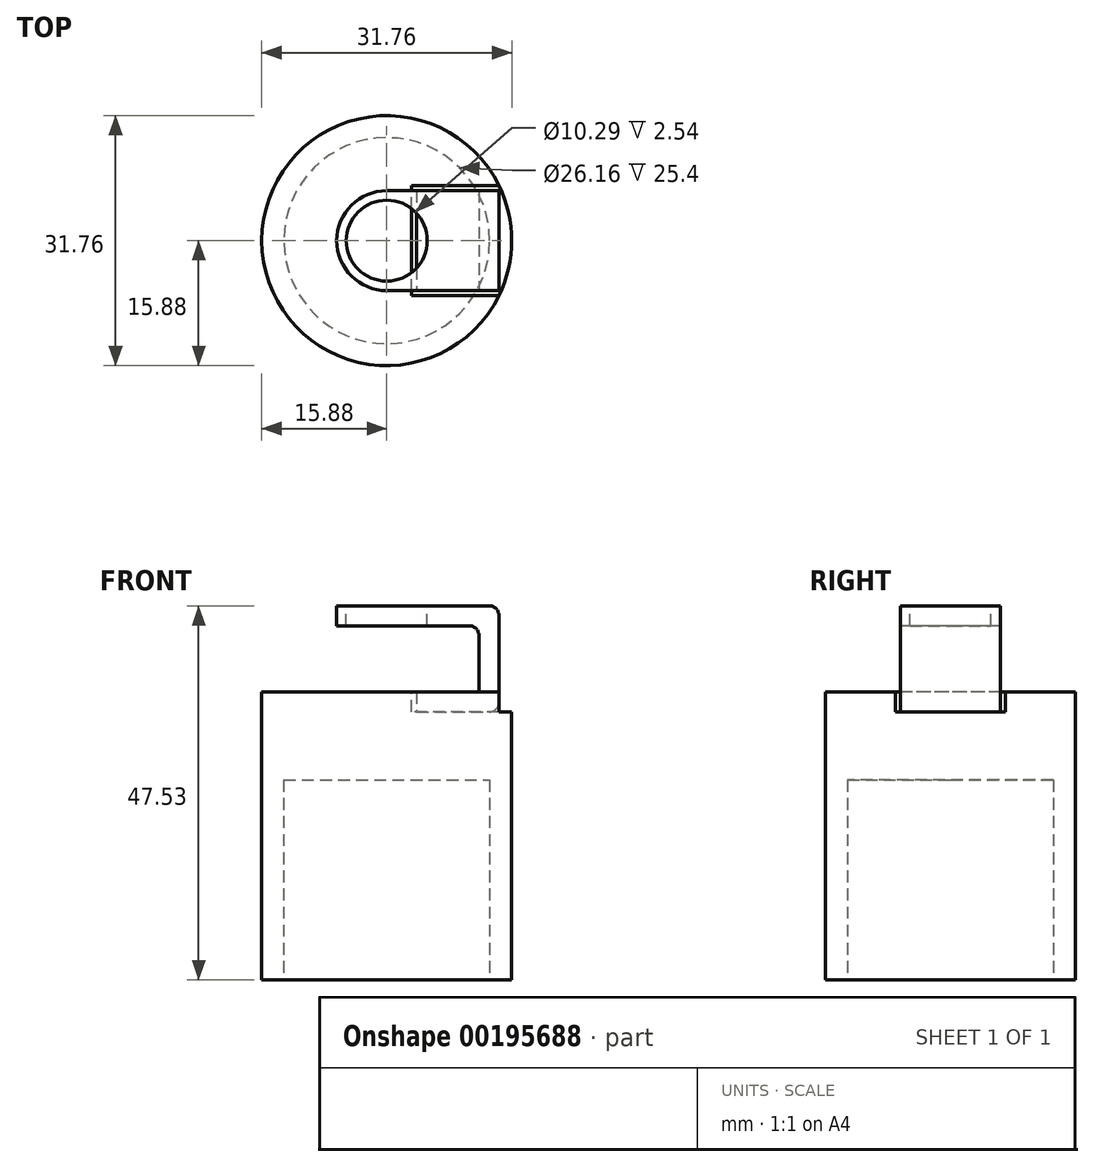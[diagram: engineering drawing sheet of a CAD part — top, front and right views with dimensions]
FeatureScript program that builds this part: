
annotation { "Feature Type Name" : "Feature", "Feature Type Description" : "" }
export const myFeature = defineFeature(function(context is Context, id is Id, definition is map)
    precondition{}
    {
        {
            var Q0;
            Q0=qCreatedBy(makeId("Top.planeOp"),FACE);
            var sketch = newSketch(context, id + "F0", { "sketchPlane" : qUnion([Q0])});
            skCircle(sketch, "E0", {"center": v(0, 0) * mm, "radius": 15.88 * mm});
            skSolve(sketch);
        }
        {
            var Q0;
            Q0 = qSketchRegion(id + "F0", true);
            extrude(context, id + "F1", {"entities" : qUnion([Q0]), "depth" : 36.58 * mm, "offsetDistance" : 25.4 * mm});
        }
        {
            var Q0;
            Q0=makeQuery(id+"F1.opExtrude","CAP_FACE",FACE,{"disambiguationData":[OSD([sQuery(id+"F0.wireOp",EDGE,"E0")])],"isStart":true});
            var sketch = newSketch(context, id + "F2", { "sketchPlane" : qUnion([Q0])});
            skCircle(sketch, "E1", {"center": v(0, 0) * mm, "radius": 13.08 * mm});
            skSolve(sketch);
        }
        {
            var Q0;
            Q0 = qSketchRegion(id + "F2", true);
            extrude(context, id + "F3", {"entities" : qUnion([Q0]), "operationType" : NewBodyOperationType.REMOVE, "oppositeDirection" : true, "depth" : 25.4 * mm, "offsetDistance" : 25.4 * mm});
        }
        {
            var Q0;
            Q0=makeQuery(id+"F1.opExtrude","CAP_FACE",FACE,{"disambiguationData":[OSD([sQuery(id+"F0.wireOp",EDGE,"E0")])],"isStart":false});
            var sketch = newSketch(context, id + "F4", { "sketchPlane" : qUnion([Q0])});
            skLineSegment(sketch, "E2.bottom", {"start": v(28.57, -6.98) * mm, "end": v(3.17, -6.99) * mm});
            skLineSegment(sketch, "E2.top", {"start": v(28.57, 6.99) * mm, "end": v(3.17, 6.99) * mm});
            skLineSegment(sketch, "E2.left", {"start": v(28.57, -6.99) * mm, "end": v(28.57, 6.99) * mm});
            skLineSegment(sketch, "E2.right", {"start": v(3.17, -6.99) * mm, "end": v(3.17, 6.99) * mm});
            skPoint(sketch, "E2.middle", {"position": v(15.88, 0) * mm});
            skSolve(sketch);
        }
        {
            var Q0;
            Q0 = qSketchRegion(id + "F4", true);
            extrude(context, id + "F5", {"entities" : qUnion([Q0]), "operationType" : NewBodyOperationType.REMOVE, "oppositeDirection" : true, "depth" : 2.54 * mm, "offsetDistance" : 25.4 * mm});
        }
        {
            var Q0;
            Q0=makeQuery(id+"F5.boolean.opBoolean","COPY",FACE,{"derivedFrom":makeQuery(id+"F5.opExtrude","CAP_FACE",FACE,{"disambiguationData":[OSD([sQuery(id+"F4.wireOp",EDGE,"E2.bottom"),sQuery(id+"F4.wireOp",EDGE,"E2.top"),sQuery(id+"F4.wireOp",EDGE,"E2.left"),sQuery(id+"F4.wireOp",EDGE,"E2.right")])],"isStart":false})});
            var sketch = newSketch(context, id + "F6", { "sketchPlane" : qUnion([Q0])});
            skLineSegment(sketch, "E3.bottom", {"start": v(3.8, 6.35) * mm, "end": v(14.26, 6.35) * mm});
            skLineSegment(sketch, "E3.top", {"start": v(3.8, -6.35) * mm, "end": v(14.26, -6.35) * mm});
            skLineSegment(sketch, "E3.left", {"start": v(3.8, 6.35) * mm, "end": v(3.8, -6.35) * mm});
            skLineSegment(sketch, "E3.right", {"start": v(14.26, 6.35) * mm, "end": v(14.26, -6.35) * mm});
            skPoint(sketch, "E4", {"position": v(14.26, 0) * mm});
            skSolve(sketch);
        }
        {
            var Q0;
            Q0 = qSketchRegion(id + "F6", true);
            extrude(context, id + "F7", {"entities" : qUnion([Q0]), "depth" : 2.54 * mm, "offsetDistance" : 25.4 * mm});
        }
        {
            var Q0;
            Q0=makeQuery(id+"F7.opExtrude","CAP_FACE",FACE,{"disambiguationData":[OSD([sQuery(id+"F6.wireOp",EDGE,"E3.bottom"),sQuery(id+"F6.wireOp",EDGE,"E3.top"),sQuery(id+"F6.wireOp",EDGE,"E3.left"),sQuery(id+"F6.wireOp",EDGE,"E3.right")])],"isStart":false});
            var sketch = newSketch(context, id + "F8", { "sketchPlane" : qUnion([Q0])});
            skLineSegment(sketch, "E5.bottom", {"start": v(11.72, 6.35) * mm, "end": v(14.26, 6.35) * mm});
            skLineSegment(sketch, "E5.top", {"start": v(11.72, -6.35) * mm, "end": v(14.26, -6.35) * mm});
            skLineSegment(sketch, "E5.left", {"start": v(11.72, 6.35) * mm, "end": v(11.72, -6.35) * mm});
            skLineSegment(sketch, "E5.right", {"start": v(14.26, 6.35) * mm, "end": v(14.26, -6.35) * mm});
            skSolve(sketch);
        }
        {
            var Q0;
            Q0 = qSketchRegion(id + "F8", true);
            extrude(context, id + "F9", {"entities" : qUnion([Q0]), "operationType" : NewBodyOperationType.ADD, "depth" : 10.95 * mm, "offsetDistance" : 25.4 * mm});
        }
        {
            var Q0;
            Q0=makeQuery(id+"F9.opExtrude","CAP_FACE",FACE,{"disambiguationData":[OSD([sQuery(id+"F8.wireOp",EDGE,"E5.bottom"),sQuery(id+"F8.wireOp",EDGE,"E5.top"),sQuery(id+"F8.wireOp",EDGE,"E5.left"),sQuery(id+"F8.wireOp",EDGE,"E5.right")])],"isStart":false});
            var sketch = newSketch(context, id + "F10", { "sketchPlane" : qUnion([Q0])});
            skCircle(sketch, "E6", {"center": v(0, 0) * mm, "radius": 5.14 * mm});
            skLineSegment(sketch, "E7.bottom", {"start": v(14.26, 6.35) * mm, "end": v(0, 6.35) * mm});
            skLineSegment(sketch, "E7.top", {"start": v(14.26, -6.35) * mm, "end": v(0, -6.35) * mm});
            skLineSegment(sketch, "E7.left", {"start": v(14.26, 6.35) * mm, "end": v(14.26, -6.35) * mm});
            skArc(sketch, "E8", {"start": v(0, 6.35) * mm, "mid": v(-6.35, 0) * mm, "end": v(0, -6.35) * mm});
            skSolve(sketch);
        }
        {
            var Q0;
            Q0 = qSketchRegion(id + "F10", true);
            extrude(context, id + "F11", {"entities" : qUnion([Q0]), "operationType" : NewBodyOperationType.ADD, "oppositeDirection" : true, "depth" : 2.54 * mm, "offsetDistance" : 25.4 * mm});
        }
        {
            var Q0;
            Q0=makeQuery(id+"F9.opExtrude","CAP_EDGE",EDGE,{"disambiguationData":[OSD([sQuery(id+"F8.wireOp",EDGE,"E5.right")])],"isStart":false});
            var Q1;
            Q1=makeQuery(id+"F11.boolean.opBoolean","INTERSECT",EDGE,{"derivedFrom":[makeQuery(id+"F9.opExtrude","SWEPT_FACE",FACE,{"disambiguationData":[OSD([sQuery(id+"F8.wireOp",EDGE,"E5.left")])]}),makeQuery(id+"F11.opExtrude","CAP_FACE",FACE,{"disambiguationData":[OSD([sQuery(id+"F10.wireOp",EDGE,"E6"),sQuery(id+"F10.wireOp",EDGE,"E7.bottom"),sQuery(id+"F10.wireOp",EDGE,"E7.top"),sQuery(id+"F10.wireOp",EDGE,"E7.left"),sQuery(id+"F10.wireOp",EDGE,"E8")])],"isStart":false})]});
            var Q2;
            Q2=makeQuery(id+"F7.opExtrude","CAP_EDGE",EDGE,{"disambiguationData":[OSD([sQuery(id+"F6.wireOp",EDGE,"E3.right")])],"isStart":true});
            var Q3;
            Q3=makeQuery(id+"F9.opExtrude","CAP_EDGE",EDGE,{"disambiguationData":[OSD([sQuery(id+"F8.wireOp",EDGE,"E5.left")])],"isStart":true});
            fillet(context, id + "F12", {"entities" : qUnion([Q0, Q1, Q2, Q3]), "tangentPropagation" : true, "radius" : 1.27 * mm, "defaultsChanged" : false, "vertexSettings" : [], "allowEdgeOverflow" : false});
        }
    });
